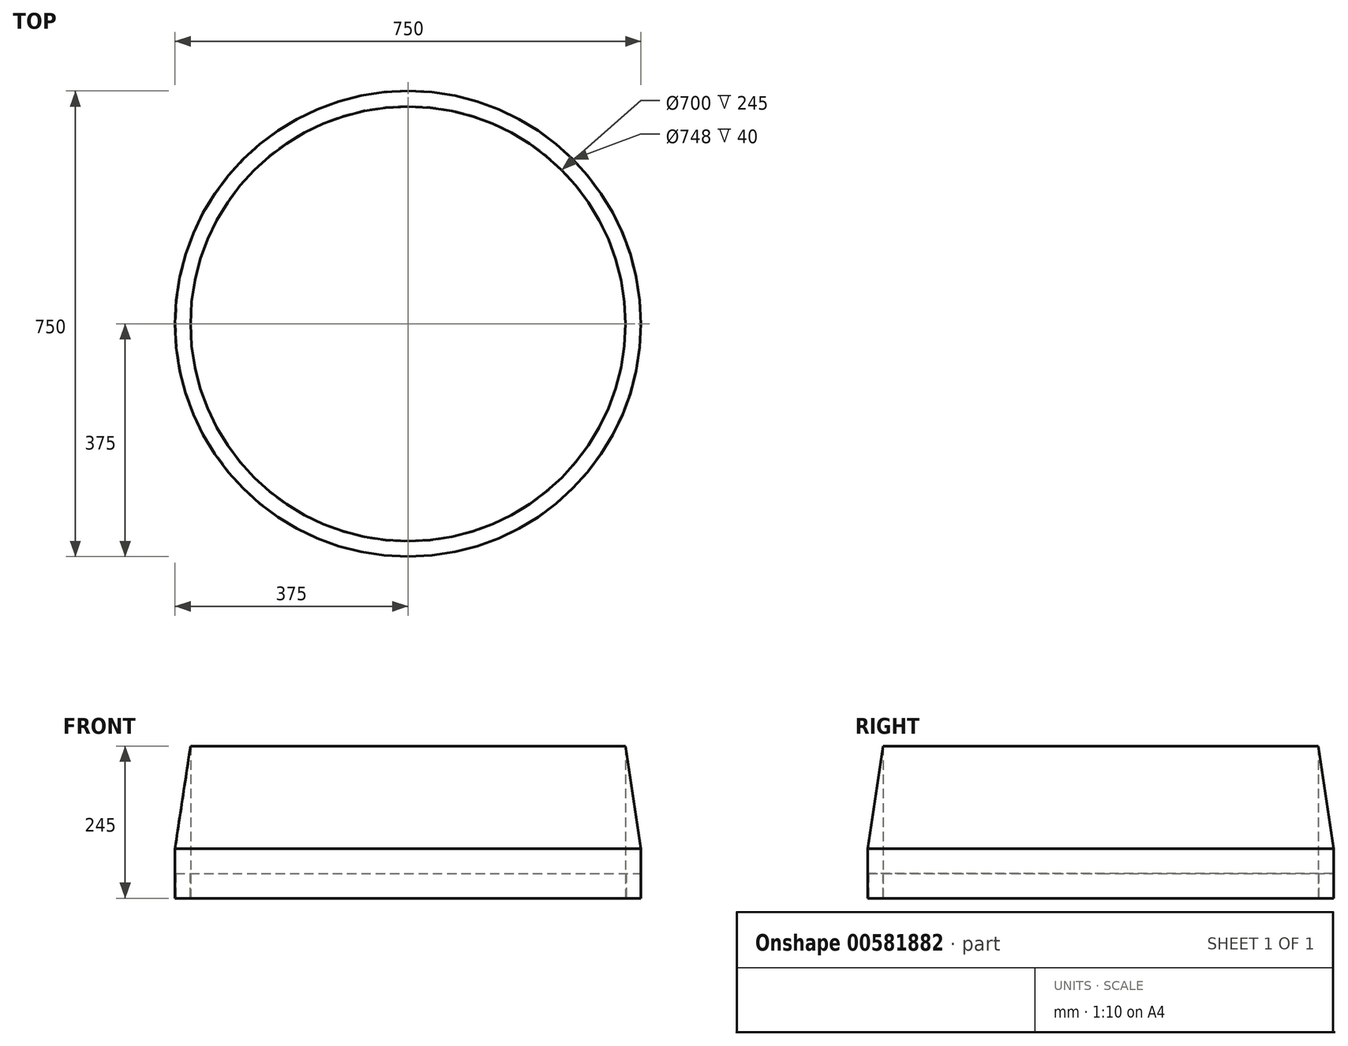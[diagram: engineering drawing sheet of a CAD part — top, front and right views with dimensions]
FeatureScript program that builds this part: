
annotation { "Feature Type Name" : "Feature", "Feature Type Description" : "" }
export const myFeature = defineFeature(function(context is Context, id is Id, definition is map)
    precondition{}
    {
        {
            var Q0;
            Q0=qCreatedBy(makeId("Front.planeOp"),FACE);
            var sketch = newSketch(context, id + "F0", { "sketchPlane" : qUnion([Q0])});
            skLineSegment(sketch, "E0", {"start": v(0, -139.25) * mm, "end": v(0, 240.83) * mm, "construction": true});
            skLineSegment(sketch, "E1", {"start": v(-350, -67.22) * mm, "end": v(-350, 177.78) * mm});
            skLineSegment(sketch, "E2", {"start": v(-350, 177.78) * mm, "end": v(-375, 12.78) * mm});
            skLineSegment(sketch, "E3", {"start": v(-375, 12.78) * mm, "end": v(-375, -67.22) * mm});
            skLineSegment(sketch, "E4", {"start": v(-375, -67.22) * mm, "end": v(-374, -67.22) * mm});
            skLineSegment(sketch, "E5", {"start": v(-374, -67.22) * mm, "end": v(-374, -27.22) * mm});
            skLineSegment(sketch, "E6", {"start": v(-374, -27.22) * mm, "end": v(-351, -27.22) * mm});
            skLineSegment(sketch, "E7", {"start": v(-351, -27.22) * mm, "end": v(-351, -67.22) * mm});
            skLineSegment(sketch, "E8", {"start": v(-351, -67.22) * mm, "end": v(-350, -67.22) * mm});
            skSolve(sketch);
        }
        {
            var Q0;
            Q0=qSketchRegion(id+"F0",true);
            var Q1;
            Q1=sQuery(id+"F0.wireOp",EDGE,"E0");
            revolve(context, id + "F1", {"entities" : qUnion([Q0]), "axis" : qUnion([Q1]), "revolveType" : RevolveType.FULL});
        }
    });
